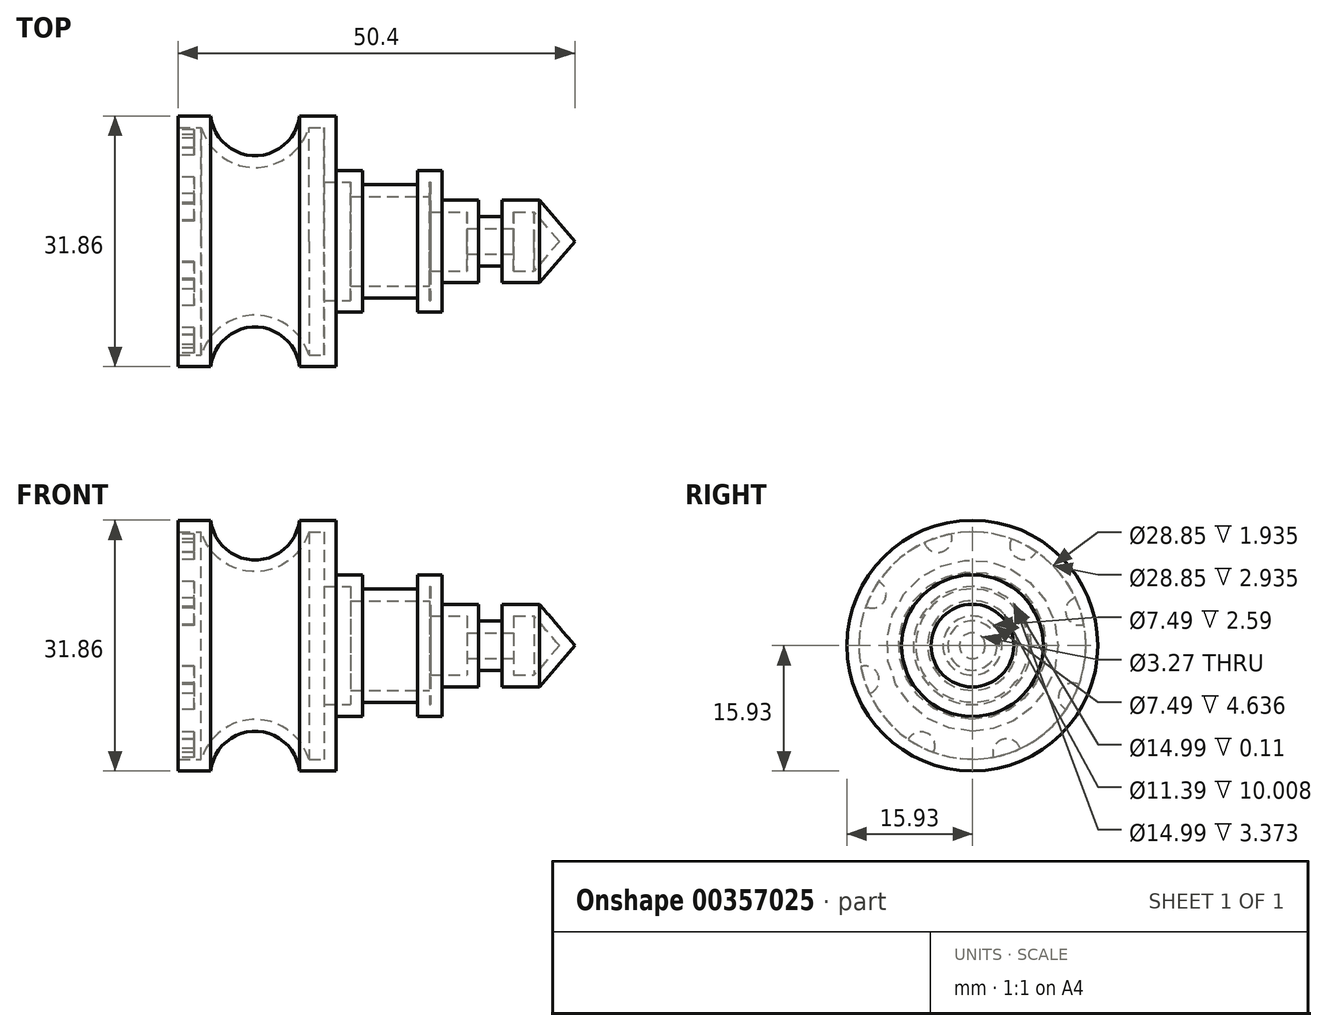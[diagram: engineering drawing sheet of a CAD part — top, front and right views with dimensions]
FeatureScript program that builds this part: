
annotation { "Feature Type Name" : "Feature", "Feature Type Description" : "" }
export const myFeature = defineFeature(function(context is Context, id is Id, definition is map)
    precondition{}
    {
        {
            var Q0;
            Q0=qCreatedBy(makeId("Front.planeOp"),FACE);
            var sketch = newSketch(context, id + "F0", { "sketchPlane" : qUnion([Q0])});
            skLineSegment(sketch, "E0", {"start": v(0, 15.93) * mm, "end": v(4.15, 15.93) * mm});
            skLineSegment(sketch, "E1", {"start": v(20.05, 15.93) * mm, "end": v(20.05, 9) * mm});
            skLineSegment(sketch, "E2", {"start": v(20.05, 9) * mm, "end": v(23.42, 9) * mm});
            skLineSegment(sketch, "E3", {"start": v(33.54, 9) * mm, "end": v(33.54, 5.25) * mm});
            skLineSegment(sketch, "E4", {"start": v(33.54, 5.25) * mm, "end": v(38.18, 5.25) * mm});
            skLineSegment(sketch, "E5", {"start": v(45.9, 5.25) * mm, "end": v(50.4, 0) * mm});
            skLineSegment(sketch, "E6", {"start": v(0, 0) * mm, "end": v(68.4, 0) * mm, "construction": true});
            skLineSegment(sketch, "E7", {"start": v(0, 15.93) * mm, "end": v(0, 0) * mm});
            skLineSegment(sketch, "E8", {"start": v(50.4, 0) * mm, "end": v(0, 0) * mm});
            skArc(sketch, "E9", {"start": v(4.15, 15.93) * mm, "mid": v(9.77, 10.88) * mm, "end": v(15.4, 15.93) * mm});
            skLineSegment(sketch, "E10.trimOffspring", {"start": v(15.4, 15.93) * mm, "end": v(20.05, 15.93) * mm});
            skLineSegment(sketch, "E11.top", {"start": v(23.42, 7.2) * mm, "end": v(30.43, 7.2) * mm});
            skLineSegment(sketch, "E11.left", {"start": v(23.42, 9) * mm, "end": v(23.42, 7.2) * mm});
            skLineSegment(sketch, "E11.right", {"start": v(30.43, 9) * mm, "end": v(30.43, 7.2) * mm});
            skLineSegment(sketch, "E12.trimOffspring", {"start": v(30.43, 9) * mm, "end": v(33.54, 9) * mm});
            skLineSegment(sketch, "E13.top", {"start": v(38.18, 3.14) * mm, "end": v(41.13, 3.14) * mm});
            skLineSegment(sketch, "E13.left", {"start": v(38.18, 5.25) * mm, "end": v(38.18, 3.14) * mm});
            skLineSegment(sketch, "E13.right", {"start": v(41.13, 5.25) * mm, "end": v(41.13, 3.14) * mm});
            skLineSegment(sketch, "E14.trimOffspring", {"start": v(41.13, 5.25) * mm, "end": v(45.9, 5.25) * mm});
            skSolve(sketch);
        }
        {
            var Q0;
            Q0=makeQuery(id+"F0.imprint","IMPRINT",FACE,{"disambiguationData":[TD([[makeQuery(id+"F0.imprint","IMPRINT",EDGE,{"derivedFrom":sQuery(id+"F0.wireOp",EDGE,"E0")}),-1.0]])]});
            var Q1;
            Q1=sQuery(id+"F0.wireOp",EDGE,"E8");
            revolve(context, id + "F1", {"entities" : qUnion([Q0]), "axis" : qUnion([Q1]), "revolveType" : RevolveType.FULL});
        }
        {
            var Q0;
            Q0=makeQuery(id+"F1.opRevolve","SWEPT_FACE",FACE,{"disambiguationData":[OSD([sQuery(id+"F0.wireOp",EDGE,"E7")])]});
            shell(context, id + "F2", {"entities" : qUnion([Q0]), "thickness" : 1.5 * mm});
        }
        {
            var Q0;
            Q0=makeQuery(id+"F1.opRevolve","SWEPT_FACE",FACE,{"disambiguationData":[OSD([sQuery(id+"F0.wireOp",EDGE,"E7")])]});
            var sketch = newSketch(context, id + "F3", { "sketchPlane" : qUnion([Q0])});
            skCircle(sketch, "E15.0", {"center": v(0, 0) * mm, "radius": 14.43 * mm});
            skCircle(sketch, "E15.1", {"center": v(0, 0) * mm, "radius": 15.93 * mm});
            skArc(sketch, "E16", {"start": v(-8.13, 11.92) * mm, "mid": v(-5.72, 11.14) * mm, "end": v(-4.95, 13.55) * mm});
            skArc(sketch, "E17", {"start": v(-4.95, 13.55) * mm, "mid": v(-6.6, 12.83) * mm, "end": v(-8.13, 11.92) * mm});
            skSolve(sketch);
        }
        {
            var Q0;
            Q0=makeQuery(id+"F3.imprint","IMPRINT",FACE,{"disambiguationData":[TD([[makeQuery(id+"F3.imprint","IMPRINT",EDGE,{"derivedFrom":sQuery(id+"F3.wireOp",EDGE,"E16")}),1.0]])]});
            extrude(context, id + "F4", {"entities" : qUnion([Q0]), "oppositeDirection" : true, "depth" : 2 * mm});
        }
        {
            var Q0;
            Q0=makeQuery(id+"F4.opExtrude","SWEPT_BODY",BODY,{"disambiguationData":[OSD([sQuery(id+"F3.wireOp",EDGE,"E16"),sQuery(id+"F3.wireOp",EDGE,"E17")])]});
            var Q1;
            Q1=makeQuery(id+"F2.opShell","OFFSET_EDGE",EDGE,{"disambiguationData":[OSD([sQuery(id+"F0.wireOp",EDGE,"E0"),sQuery(id+"F0.wireOp",EDGE,"E7")])]});
            circularPattern(context, id + "F5", {"entities" : qUnion([Q0]), "axis" : qUnion([Q1]), "angle" : 360 * degree, "instanceCount" : 8, "equalSpace" : true});
        }
    });
